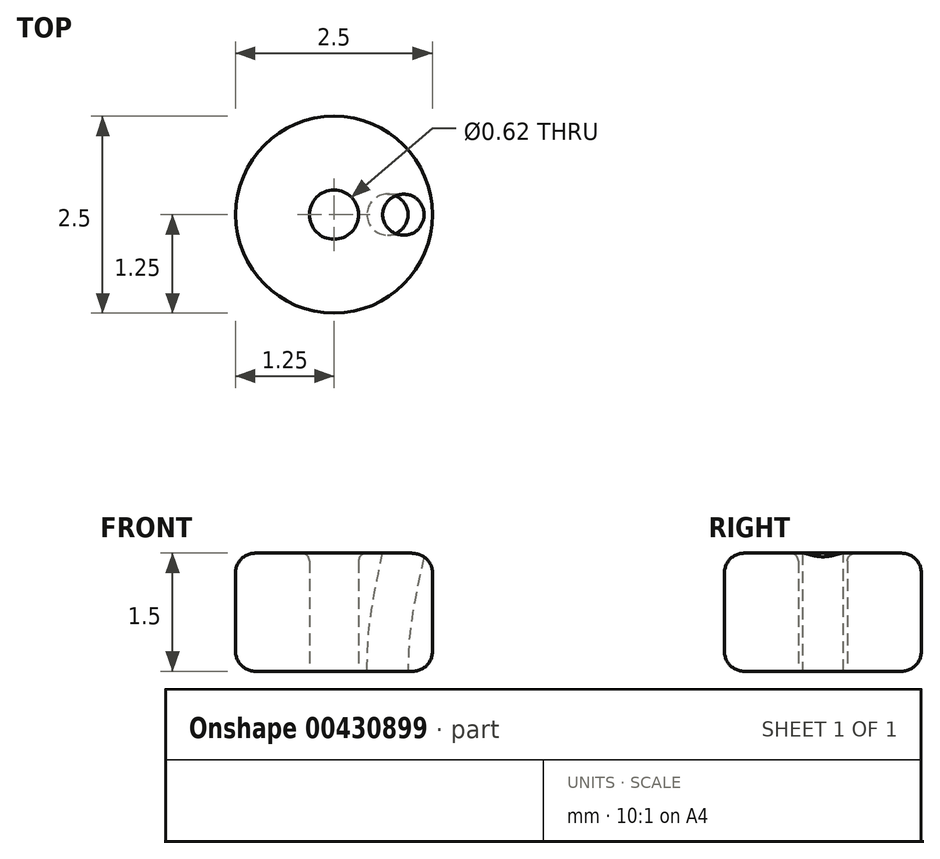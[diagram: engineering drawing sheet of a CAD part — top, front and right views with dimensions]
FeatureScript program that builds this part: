
annotation { "Feature Type Name" : "Feature", "Feature Type Description" : "" }
export const myFeature = defineFeature(function(context is Context, id is Id, definition is map)
    precondition{}
    {
        {
            var Q0;
            Q0=qCreatedBy(makeId("Front.planeOp"),FACE);
            var sketch = newSketch(context, id + "F0", { "sketchPlane" : qUnion([Q0])});
            skLineSegment(sketch, "E0.bottom", {"start": v(0, 2) * mm, "end": v(1.25, 2) * mm});
            skLineSegment(sketch, "E0.left", {"start": v(0, 2) * mm, "end": v(0, 0.5) * mm});
            skLineSegment(sketch, "E1", {"start": v(0, 40.9) * mm, "end": v(0, 2) * mm, "construction": true});
            skLineSegment(sketch, "E2", {"start": v(1.25, 2) * mm, "end": v(1.25, 0.5) * mm});
            skLineSegment(sketch, "E3", {"start": v(1.25, 0.5) * mm, "end": v(0, 0.5) * mm});
            skPoint(sketch, "E4.end.orphan", {"position": v(0, 0) * mm});
            skSolve(sketch);
        }
        {
            var Q0;
            Q0=makeQuery(id+"F0.imprint","IMPRINT",FACE,{"disambiguationData":[TD([[makeQuery(id+"F0.imprint","IMPRINT",EDGE,{"derivedFrom":sQuery(id+"F0.wireOp",EDGE,"E0.bottom")}),-1.0]])]});
            var Q1;
            Q1=sQuery(id+"F0.wireOp",EDGE,"E1");
            revolve(context, id + "F1", {"entities" : qUnion([Q0]), "axis" : qUnion([Q1]), "revolveType" : RevolveType.FULL});
        }
        {
            var Q0;
            Q0=makeQuery(id+"F1.opRevolve","SWEPT_EDGE",EDGE,{"disambiguationData":[OSD([sQuery(id+"F0.wireOp",EDGE,"E2"),sQuery(id+"F0.wireOp",EDGE,"E3")])]});
            var Q1;
            Q1=makeQuery(id+"F1.opRevolve","SWEPT_EDGE",EDGE,{"disambiguationData":[OSD([sQuery(id+"F0.wireOp",EDGE,"E0.bottom"),sQuery(id+"F0.wireOp",EDGE,"E2")])]});
            fillet(context, id + "F2", {"entities" : qUnion([Q0, Q1]), "radius" : .25 * mm, "tangentPropagation" : true, "allowEdgeOverflow" : false});
        }
        {
            var Q0;
            Q0=qCreatedBy(makeId("Front.planeOp"),FACE);
            var sketch = newSketch(context, id + "F3", { "sketchPlane" : qUnion([Q0])});
            skFitSpline(sketch, "E5", {"points": [v(0.68, 0.5) * mm, v(0.73, 1.18) * mm, v(0.9, 2.07) * mm], "startDerivative": vector(0.06, 2.17) * mm, "endDerivative": vector(0.2, 0.6) * mm});
            skSolve(sketch);
        }
        {
            var Q0;
            Q0=makeQuery(id+"F1.opRevolve","SWEPT_FACE",FACE,{"disambiguationData":[OSD([sQuery(id+"F0.wireOp",EDGE,"E3")])]});
            var sketch = newSketch(context, id + "F4", { "sketchPlane" : qUnion([Q0])});
            skCircle(sketch, "E6", {"center": v(0.68, 0) * mm, "radius": 0.26 * mm});
            skSolve(sketch);
        }
        {
            var Q0;
            Q0 = qSketchRegion(id + "F4", true);
            var Q1;
            Q1 = qConstructionFilter(qBodyType(qCreatedBy(id + "F3" ,EDGE), BodyType.WIRE), ConstructionObject.NO);
            sweep(context, id + "F5", {"operationType" : NewBodyOperationType.REMOVE, "profiles" : qUnion([Q0]), "path" : qUnion([Q1])});
        }
        {
            var Q0;
            Q0=makeQuery(id+"F4.imprint","IMPRINT",FACE,{"disambiguationData":[TD([[makeQuery(id+"F4.imprint","IMPRINT",EDGE,{"derivedFrom":sQuery(id+"F4.wireOp",EDGE,"E6")}),-1.0]])]});
            var sketch = newSketch(context, id + "F6", { "sketchPlane" : qUnion([Q0])});
            skCircle(sketch, "E7", {"center": v(0, 0) * mm, "radius": 1.04 * mm});
            skSolve(sketch);
        }
        {
            var Q0;
            Q0=makeQuery(id+"F6.imprint","IMPRINT",FACE,{"disambiguationData":[TD([[makeQuery(id+"F6.imprint","IMPRINT",EDGE,{"derivedFrom":makeQuery(id+"F4.imprint","IMPRINT",EDGE,{"derivedFrom":sQuery(id+"F4.wireOp",EDGE,"E6")})}),-1.0]])]});
            var sketch = newSketch(context, id + "F7", { "sketchPlane" : qUnion([Q0])});
            skCircle(sketch, "E8", {"center": v(0, 0) * mm, "radius": 0.31 * mm});
            skCircle(sketch, "E9", {"center": v(0, 0.18) * mm, "radius": 0.13 * mm});
            skSolve(sketch);
        }
        {
            var Q0;
            Q0=makeQuery(id+"F7.imprint","IMPRINT",FACE,{"disambiguationData":[TD([[makeQuery(id+"F7.imprint","IMPRINT",EDGE,{"derivedFrom":sQuery(id+"F7.wireOp",EDGE,"E9")}),1.0]])]});
            var Q1;
            Q1=makeQuery(id+"F7.imprint","IMPRINT",FACE,{"disambiguationData":[TD([[makeQuery(id+"F7.imprint","IMPRINT",EDGE,{"derivedFrom":sQuery(id+"F7.wireOp",EDGE,"E8")}),1.0]])]});
            extrude(context, id + "F8", {"entities" : qUnion([Q0, Q1]), "operationType" : NewBodyOperationType.REMOVE, "endBound" : BoundingType.THROUGH_ALL, "oppositeDirection" : true, "depth" : 25 * mm});
        }
        {
            var Q0;
            Q0=makeQuery(id+"F8.boolean.opBoolean","INTERSECT",EDGE,{"derivedFrom":[makeQuery(id+"F1.opRevolve","SWEPT_FACE",FACE,{"disambiguationData":[OSD([sQuery(id+"F0.wireOp",EDGE,"E0.bottom")])]}),makeQuery(id+"F8.opExtrude","SWEPT_FACE",FACE,{"disambiguationData":[OSD([sQuery(id+"F7.wireOp",EDGE,"E8")])]})]});
            var Q1;
            Q1=makeQuery(id+"F8.boolean.opBoolean","COPY",EDGE,{"derivedFrom":makeQuery(id+"F8.opExtrude","CAP_EDGE",EDGE,{"disambiguationData":[OSD([sQuery(id+"F7.wireOp",EDGE,"E8")])],"isStart":true})});
            fillet(context, id + "F9", {"entities" : qUnion([Q0, Q1]), "radius" : .1 * mm, "tangentPropagation" : true, "allowEdgeOverflow" : false});
        }
        {
            var Q0;
            Q0=qCreatedBy(makeId("Front.planeOp"),FACE);
            var sketch = newSketch(context, id + "F10", { "sketchPlane" : qUnion([Q0])});
            skLineSegment(sketch, "E10", {"start": v(0, 2.93) * mm, "end": v(0, -4.87) * mm, "construction": true});
            skLineSegment(sketch, "E11.bottom", {"start": v(-1.27, -0.28) * mm, "end": v(-1.02, -0.28) * mm});
            skLineSegment(sketch, "E11.top", {"start": v(-1.27, -9.58) * mm, "end": v(-1.02, -9.58) * mm});
            skLineSegment(sketch, "E11.left", {"start": v(-1.27, -0.28) * mm, "end": v(-1.27, -9.58) * mm});
            skLineSegment(sketch, "E11.right", {"start": v(-1.02, -0.28) * mm, "end": v(-1.02, -9.58) * mm});
            skSolve(sketch);
        }
        {
            var Q0;
            Q0=makeQuery(id+"F10.imprint","IMPRINT",FACE,{"disambiguationData":[TD([[makeQuery(id+"F10.imprint","IMPRINT",EDGE,{"derivedFrom":sQuery(id+"F10.wireOp",EDGE,"E11.bottom")}),-1.0]])]});
            var Q1;
            Q1=sQuery(id+"F10.wireOp",EDGE,"E10");
            revolve(context, id + "F11", {"entities" : qUnion([Q0]), "axis" : qUnion([Q1]), "revolveType" : RevolveType.FULL});
        }
        {
            var Q0;
            Q0=qCreatedBy(makeId("Front.planeOp"),FACE);
            var sketch = newSketch(context, id + "F12", { "sketchPlane" : qUnion([Q0])});
            skFitSpline(sketch, "E12", {"points": [v(0.68, -9.58) * mm, v(0.68, 0.5) * mm, v(0.7, 1.14) * mm, v(0.92, 2.1) * mm, v(2.59, 6.73) * mm, v(2.77, 7.3) * mm], "startDerivative": vector(-0.05, 1.8) * mm, "endDerivative": vector(0.67, 2.53) * mm});
            skSolve(sketch);
        }
        {
            var Q0;
            Q0=makeQuery(id+"F11.opRevolve","SWEPT_FACE",FACE,{"disambiguationData":[OSD([sQuery(id+"F10.wireOp",EDGE,"E11.top")])]});
            var sketch = newSketch(context, id + "F13", { "sketchPlane" : qUnion([Q0])});
            skCircle(sketch, "E13", {"center": v(0.68, 0) * mm, "radius": 0.2 * mm});
            skSolve(sketch);
        }
        {
            var Q0;
            Q0=makeQuery(id+"F13.imprint","IMPRINT",FACE,{"disambiguationData":[TD([[makeQuery(id+"F13.imprint","IMPRINT",EDGE,{"derivedFrom":sQuery(id+"F13.wireOp",EDGE,"E13")}),1.0]])]});
            var Q1;
            Q1 = qConstructionFilter(qBodyType(qCreatedBy(id + "F12" ,EDGE), BodyType.WIRE), ConstructionObject.NO);
            sweep(context, id + "F14", {"profiles" : qUnion([Q0]), "path" : qUnion([Q1])});
        }
        {
            var Q0;
            Q0=makeQuery(id+"F11.opRevolve","SWEPT_BODY",BODY,{"disambiguationData":[OSD([sQuery(id+"F10.wireOp",EDGE,"E11.bottom"),sQuery(id+"F10.wireOp",EDGE,"E11.top"),sQuery(id+"F10.wireOp",EDGE,"E11.left"),sQuery(id+"F10.wireOp",EDGE,"E11.right")])]});
            deleteBodies(context, id + "F15", {"entities" : qUnion([Q0])});
        }
        {
            var Q0;
            Q0=makeQuery(id+"F14.opSweep","SWEPT_BODY",BODY,{"disambiguationData":[OSD([sQuery(id+"F12.wireOp",EDGE,"E12"),sQuery(id+"F13.wireOp",EDGE,"E13")])]});
            deleteBodies(context, id + "F16", {"entities" : qUnion([Q0])});
        }
    });
